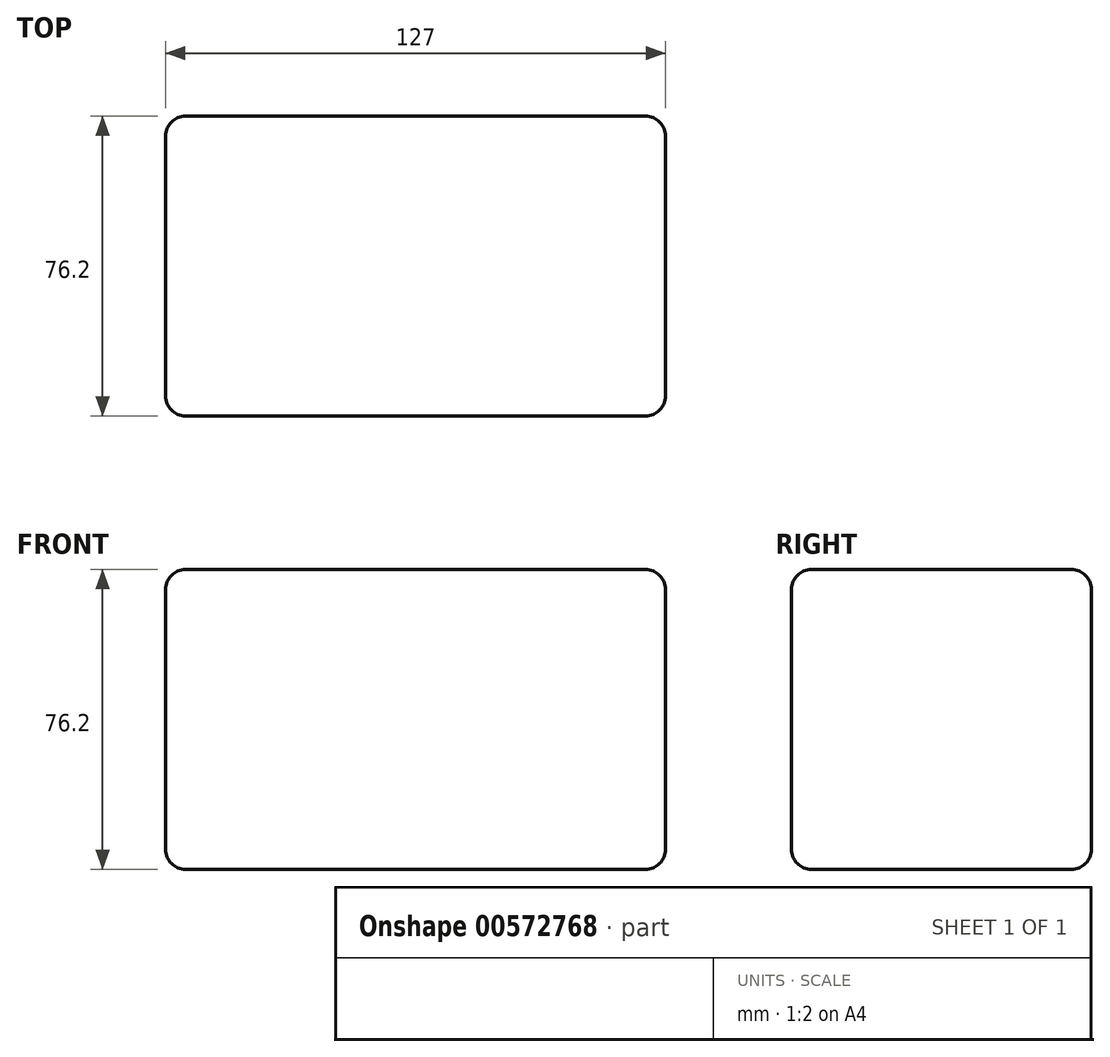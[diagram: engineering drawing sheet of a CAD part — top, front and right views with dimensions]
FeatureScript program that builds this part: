
annotation { "Feature Type Name" : "Feature", "Feature Type Description" : "" }
export const myFeature = defineFeature(function(context is Context, id is Id, definition is map)
    precondition{}
    {
        {
            var Q0;
            Q0=qCreatedBy(makeId("Front.planeOp"),FACE);
            var sketch = newSketch(context, id + "F0", { "sketchPlane" : qUnion([Q0])});
            skLineSegment(sketch, "E0.bottom", {"start": v(0, 0) * mm, "end": v(127, 0) * mm});
            skLineSegment(sketch, "E0.top", {"start": v(0, 76.2) * mm, "end": v(127, 76.2) * mm});
            skLineSegment(sketch, "E0.left", {"start": v(0, 0) * mm, "end": v(0, 76.2) * mm});
            skLineSegment(sketch, "E0.right", {"start": v(127, 0) * mm, "end": v(127, 76.2) * mm});
            skSolve(sketch);
        }
        {
            var Q0;
            Q0=makeQuery(id+"F0.imprint","IMPRINT",FACE,{"disambiguationData":[TD([[makeQuery(id+"F0.imprint","IMPRINT",EDGE,{"derivedFrom":sQuery(id+"F0.wireOp",EDGE,"E0.bottom")}),1.0]])]});
            extrude(context, id + "F1", {"entities" : qUnion([Q0]), "depth" : 76.2 * mm, "offsetDistance" : 25.4 * mm});
        }
        {
            var Q0;
            Q0=makeQuery(id+"F1.opExtrude","CAP_EDGE",EDGE,{"disambiguationData":[OSD([sQuery(id+"F0.wireOp",EDGE,"E0.top")])],"isStart":true});
            fillet(context, id + "F2", {"entities" : qUnion([Q0]), "radius" : 5.08 * mm, "tangentPropagation" : true, "allowEdgeOverflow" : false});
        }
        {
            var Q0;
            Q0=makeQuery(id+"F1.opExtrude","SWEPT_EDGE",EDGE,{"disambiguationData":[OSD([sQuery(id+"F0.wireOp",EDGE,"E0.top"),sQuery(id+"F0.wireOp",EDGE,"E0.left")])]});
            fillet(context, id + "F3", {"entities" : qUnion([Q0]), "radius" : 5.08 * mm, "tangentPropagation" : true, "allowEdgeOverflow" : false});
        }
        {
            var Q0;
            Q0=makeQuery(id+"F1.opExtrude","CAP_EDGE",EDGE,{"disambiguationData":[OSD([sQuery(id+"F0.wireOp",EDGE,"E0.top")])],"isStart":false});
            fillet(context, id + "F4", {"entities" : qUnion([Q0]), "radius" : 5.08 * mm, "tangentPropagation" : true, "allowEdgeOverflow" : false});
        }
        {
            var Q0;
            Q0=makeQuery(id+"F1.opExtrude","SWEPT_EDGE",EDGE,{"disambiguationData":[OSD([sQuery(id+"F0.wireOp",EDGE,"E0.top"),sQuery(id+"F0.wireOp",EDGE,"E0.right")])]});
            fillet(context, id + "F5", {"entities" : qUnion([Q0]), "radius" : 5.08 * mm, "tangentPropagation" : true, "allowEdgeOverflow" : false});
        }
        {
            var Q0;
            Q0=makeQuery(id+"F1.opExtrude","CAP_EDGE",EDGE,{"disambiguationData":[OSD([sQuery(id+"F0.wireOp",EDGE,"E0.bottom")])],"isStart":false});
            fillet(context, id + "F6", {"entities" : qUnion([Q0]), "radius" : 5.08 * mm, "tangentPropagation" : true, "allowEdgeOverflow" : false});
        }
    });
